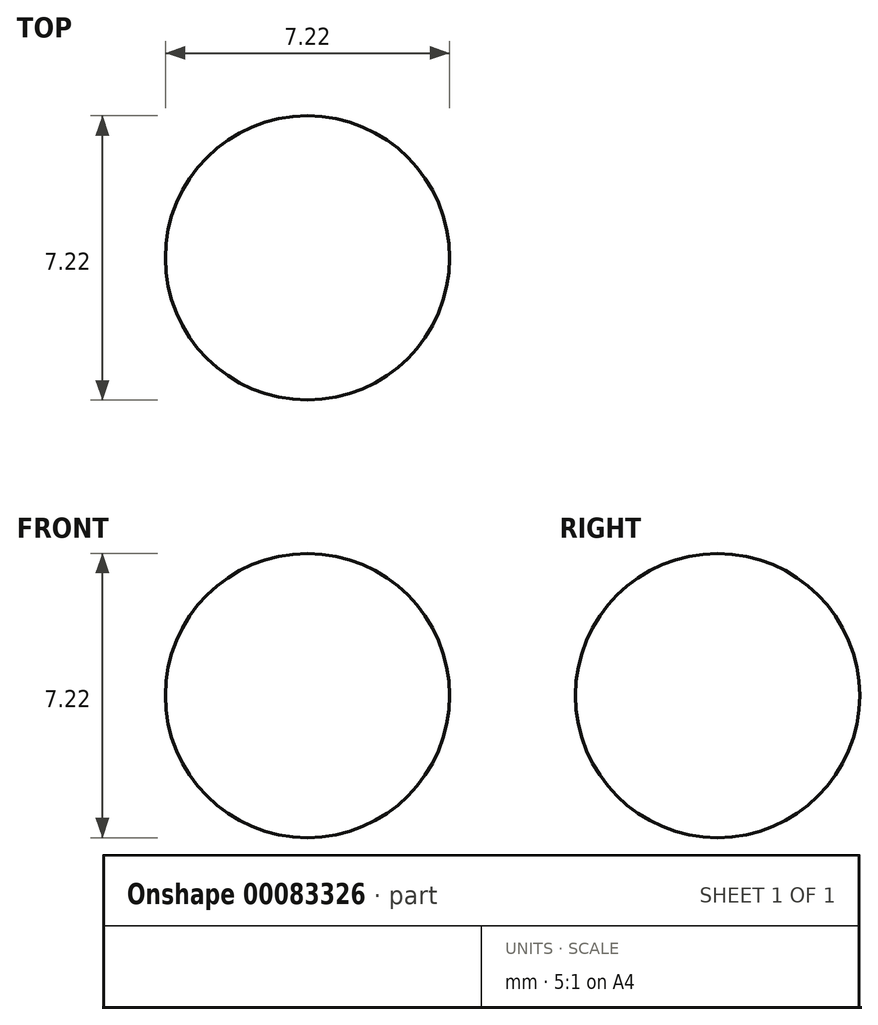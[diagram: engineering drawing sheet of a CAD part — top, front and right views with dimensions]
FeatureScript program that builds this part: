
annotation { "Feature Type Name" : "Feature", "Feature Type Description" : "" }
export const myFeature = defineFeature(function(context is Context, id is Id, definition is map)
    precondition{}
    {
        {
            var Q0;
            Q0=qCreatedBy(makeId("Top.planeOp"),FACE);
            var sketch = newSketch(context, id + "F0", { "sketchPlane" : qUnion([Q0])});
            skArc(sketch, "E0", {"start": v(0, -3.6) * mm, "mid": v(3.6, 0) * mm, "end": v(0, 3.6) * mm});
            skLineSegment(sketch, "E1", {"start": v(0, 3.6) * mm, "end": v(0, -3.6) * mm});
            skSolve(sketch);
        }
        {
            var Q0;
            Q0=makeQuery(id+"F0.imprint","IMPRINT",FACE,{"disambiguationData":[TD([[makeQuery(id+"F0.imprint","IMPRINT",EDGE,{"derivedFrom":sQuery(id+"F0.wireOp",EDGE,"E0")}),1.0]])]});
            var Q1;
            Q1=sQuery(id+"F0.wireOp",EDGE,"E0");
            var Q2;
            Q2=sQuery(id+"F0.wireOp",EDGE,"E1");
            revolve(context, id + "F1", {"entities" : qUnion([Q0]), "surfaceEntities" : qUnion([Q1]), "axis" : qUnion([Q2]), "revolveType" : RevolveType.FULL});
        }
    });
